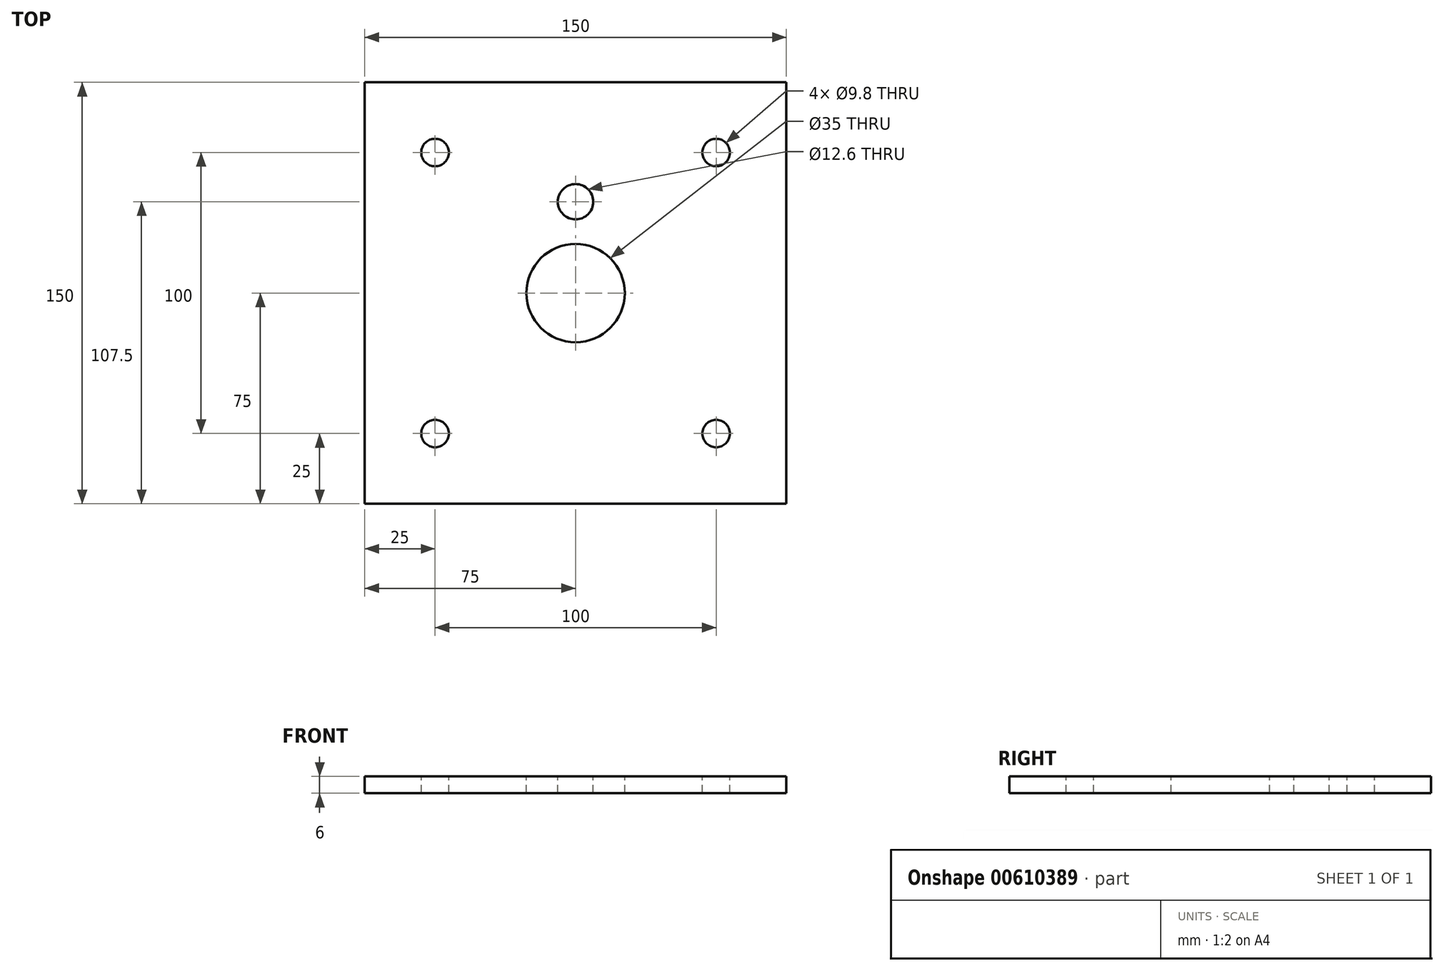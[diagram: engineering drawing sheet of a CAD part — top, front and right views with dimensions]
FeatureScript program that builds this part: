
annotation { "Feature Type Name" : "Feature", "Feature Type Description" : "" }
export const myFeature = defineFeature(function(context is Context, id is Id, definition is map)
    precondition{}
    {
        {
            var Q0;
            Q0=qCreatedBy(makeId("Top.planeOp"),FACE);
            var sketch = newSketch(context, id + "F0", { "sketchPlane" : qUnion([Q0])});
            skCircle(sketch, "E0", {"center": v(0, 0) * mm, "radius": 41.5 * mm});
            skSolve(sketch);
        }
        {
            var Q0;
            Q0=qSketchRegion(id+"F0",true);
            extrude(context, id + "F1", {"entities" : qUnion([Q0]), "depth" : 6 * mm, "offsetDistance" : 25 * mm});
        }
        {
            var Q0;
            Q0=qCreatedBy(makeId("Top.planeOp"),FACE);
            var sketch = newSketch(context, id + "F2", { "sketchPlane" : qUnion([Q0])});
            skLineSegment(sketch, "E1.bottom", {"start": v(75, 75) * mm, "end": v(-75, 75) * mm});
            skLineSegment(sketch, "E1.top", {"start": v(75, -75) * mm, "end": v(-75, -75) * mm});
            skLineSegment(sketch, "E1.left", {"start": v(75, 75) * mm, "end": v(75, -75) * mm});
            skLineSegment(sketch, "E1.right", {"start": v(-75, 75) * mm, "end": v(-75, -75) * mm});
            skPoint(sketch, "E1.middle", {"position": v(0, 0) * mm});
            skSolve(sketch);
        }
        {
            var Q0;
            Q0=makeQuery(id+"F2.imprint","IMPRINT",FACE,{"disambiguationData":[TD([[makeQuery(id+"F2.imprint","IMPRINT",EDGE,{"derivedFrom":sQuery(id+"F2.wireOp",EDGE,"E1.bottom")}),1.0]])]});
            extrude(context, id + "F3", {"entities" : qUnion([Q0]), "operationType" : NewBodyOperationType.ADD, "depth" : 6 * mm, "offsetDistance" : 25 * mm});
        }
        {
            var Q0;
            Q0=makeQuery(id+"F1.opExtrude","CAP_FACE",FACE,{"disambiguationData":[OSD([sQuery(id+"F0.wireOp",EDGE,"E0")])],"isStart":false});
            var sketch = newSketch(context, id + "F4", { "sketchPlane" : qUnion([Q0])});
            skCircle(sketch, "E2", {"center": v(0, 0) * mm, "radius": 32.5 * mm, "construction": true});
            skLineSegment(sketch, "E3", {"start": v(0, 32.5) * mm, "end": v(0, 0) * mm, "construction": true});
            skSolve(sketch);
        }
        {
            var Q0;
            Q0=makeQuery(id+"F3.boolean.opBoolean","MERGE",FACE,{"derivedFrom":[makeQuery(id+"F1.opExtrude","CAP_FACE",FACE,{"disambiguationData":[OSD([sQuery(id+"F0.wireOp",EDGE,"E0")])],"isStart":false}),makeQuery(id+"F3.opExtrude","CAP_FACE",FACE,{"disambiguationData":[OSD([sQuery(id+"F2.wireOp",EDGE,"E1.bottom"),sQuery(id+"F2.wireOp",EDGE,"E1.top"),sQuery(id+"F2.wireOp",EDGE,"E1.left"),sQuery(id+"F2.wireOp",EDGE,"E1.right")])],"isStart":false})]});
            var sketch = newSketch(context, id + "F5", { "sketchPlane" : qUnion([Q0])});
            skCircle(sketch, "E4", {"center": v(0, 0) * mm, "radius": 17.5 * mm});
            skSolve(sketch);
        }
        {
            var Q0;
            Q0=makeQuery(id+"F5.imprint","IMPRINT",FACE,{"disambiguationData":[TD([[makeQuery(id+"F5.imprint","IMPRINT",EDGE,{"derivedFrom":sQuery(id+"F5.wireOp",EDGE,"E4")}),1.0]])]});
            extrude(context, id + "F6", {"entities" : qUnion([Q0]), "operationType" : NewBodyOperationType.REMOVE, "endBound" : BoundingType.THROUGH_ALL, "oppositeDirection" : true, "depth" : 25 * mm, "offsetDistance" : 25 * mm});
        }
        {
            var Q0;
            Q0=sQuery(id+"F4.wireOp",VERTEX,"E3.start");
            var Q1;
            Q1=makeQuery(id+"F1.opExtrude","SWEPT_BODY",BODY,{"disambiguationData":[OSD([sQuery(id+"F0.wireOp",EDGE,"E0")])]});
            hole(context, id + "F7", {"style" : HoleStyle.SIMPLE, "endStyle" : HoleEndStyle.THROUGH, "standardTappedOrClearance" : lookupTablePath({ "standard" : "ISO", "fit" : "Close", "size" : "M12", "type" : "Clearance" }), "standardBlindInLast" : lookupTablePath({ "fit" : "Close", "standard" : "ISO", "size" : "M12", "type" : "Clearance" }), "holeDiameter" : 12.6 * mm, "majorDiameter" : 5 * mm, "isTappedThrough" : true, "tappedDepth" : 12 * mm, "tapClearance" : 3, "locations" : qUnion([Q0]), "scope" : qUnion([Q1])});
        }
        {
            var Q0;
            Q0=makeQuery(id+"F3.boolean.opBoolean","MERGE",FACE,{"derivedFrom":[makeQuery(id+"F1.opExtrude","CAP_FACE",FACE,{"disambiguationData":[OSD([sQuery(id+"F0.wireOp",EDGE,"E0")])],"isStart":false}),makeQuery(id+"F3.opExtrude","CAP_FACE",FACE,{"disambiguationData":[OSD([sQuery(id+"F2.wireOp",EDGE,"E1.bottom"),sQuery(id+"F2.wireOp",EDGE,"E1.top"),sQuery(id+"F2.wireOp",EDGE,"E1.left"),sQuery(id+"F2.wireOp",EDGE,"E1.right")])],"isStart":false})]});
            var sketch = newSketch(context, id + "F8", { "sketchPlane" : qUnion([Q0])});
            skLineSegment(sketch, "E5.bottom", {"start": v(50, 50) * mm, "end": v(-50, 50) * mm});
            skLineSegment(sketch, "E5.top", {"start": v(50, -50) * mm, "end": v(-50, -50) * mm});
            skLineSegment(sketch, "E5.left", {"start": v(50, 50) * mm, "end": v(50, -50) * mm});
            skLineSegment(sketch, "E5.right", {"start": v(-50, 50) * mm, "end": v(-50, -50) * mm});
            skPoint(sketch, "E5.middle", {"position": v(0, 0) * mm});
            skSolve(sketch);
        }
        {
            var Q0;
            Q0=sQuery(id+"F8.wireOp",VERTEX,"E5.bottom.end");
            var Q1;
            Q1=sQuery(id+"F8.wireOp",VERTEX,"E5.bottom.start");
            var Q2;
            Q2=sQuery(id+"F8.wireOp",VERTEX,"E5.top.start");
            var Q3;
            Q3=sQuery(id+"F8.wireOp",VERTEX,"E5.right.end");
            var Q4;
            Q4=makeQuery(id+"F1.opExtrude","SWEPT_BODY",BODY,{"disambiguationData":[OSD([sQuery(id+"F0.wireOp",EDGE,"E0")])]});
            hole(context, id + "F9", {"style" : HoleStyle.SIMPLE, "endStyle" : HoleEndStyle.THROUGH, "standardTappedOrClearance" : lookupTablePath({ "standard" : "ANSI", "fit" : "Close", "size" : "3/8", "type" : "Clearance" }), "standardBlindInLast" : lookupTablePath({ "fit" : "Close", "standard" : "ANSI", "size" : "3/8", "type" : "Clearance" }), "holeDiameter" : 9.8 * mm, "majorDiameter" : 5 * mm, "isTappedThrough" : true, "tappedDepth" : 12 * mm, "tapClearance" : 3, "locations" : qUnion([Q0, Q1, Q2, Q3]), "scope" : qUnion([Q4])});
        }
    });
